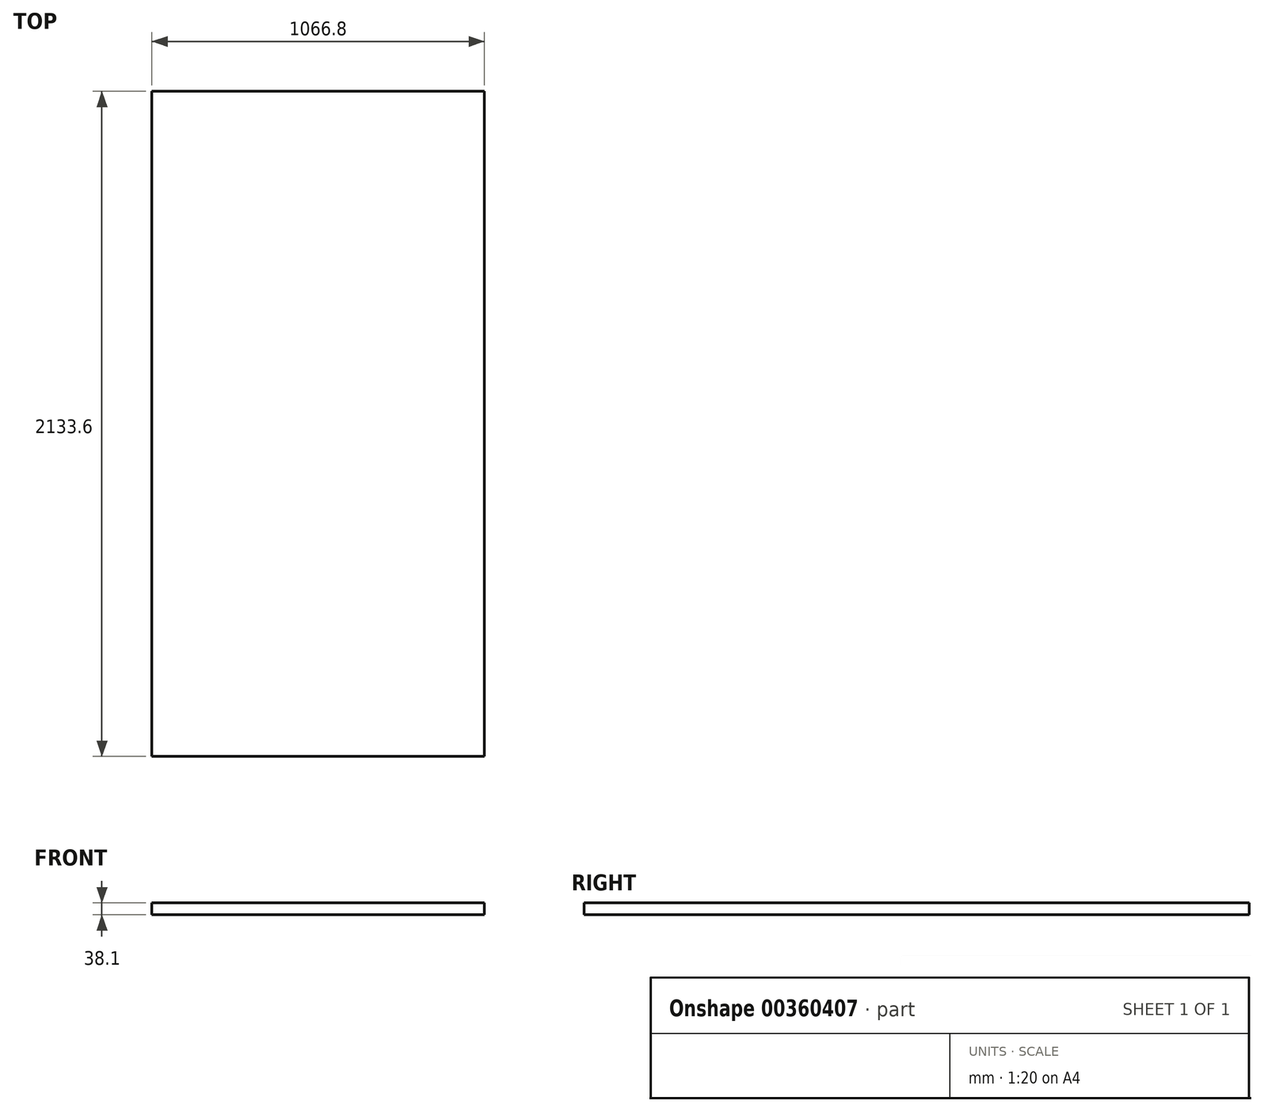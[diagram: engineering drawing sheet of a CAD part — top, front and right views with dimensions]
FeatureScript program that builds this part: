
annotation { "Feature Type Name" : "Feature", "Feature Type Description" : "" }
export const myFeature = defineFeature(function(context is Context, id is Id, definition is map)
    precondition{}
    {
        {
            var Q0;
            Q0=qCreatedBy(makeId("Top.planeOp"),FACE);
            var sketch = newSketch(context, id + "F0", { "sketchPlane" : qUnion([Q0])});
            skLineSegment(sketch, "E0.bottom", {"start": v(533.4, -1066.8) * mm, "end": v(-533.4, -1066.8) * mm});
            skLineSegment(sketch, "E0.top", {"start": v(533.4, 1066.8) * mm, "end": v(-533.4, 1066.8) * mm});
            skLineSegment(sketch, "E0.left", {"start": v(533.4, -1066.8) * mm, "end": v(533.4, 1066.8) * mm});
            skLineSegment(sketch, "E0.right", {"start": v(-533.4, -1066.8) * mm, "end": v(-533.4, 1066.8) * mm});
            skPoint(sketch, "E0.middle", {"position": v(0, 0) * mm});
            skSolve(sketch);
        }
        {
            var Q0;
            Q0=makeQuery(id+"F0.imprint","IMPRINT",FACE,{"disambiguationData":[TD([[makeQuery(id+"F0.imprint","IMPRINT",EDGE,{"derivedFrom":sQuery(id+"F0.wireOp",EDGE,"E0.bottom")}),-1.0]])]});
            var sketch = newSketch(context, id + "F1", { "sketchPlane" : qUnion([Q0])});
            skSolve(sketch);
        }
        {
            var Q0;
            Q0=makeQuery(id+"F1.imprint","IMPRINT",FACE,{"disambiguationData":[TD([[makeQuery(id+"F1.imprint","IMPRINT",EDGE,{"derivedFrom":makeQuery(id+"F0.imprint","IMPRINT",EDGE,{"derivedFrom":sQuery(id+"F0.wireOp",EDGE,"E0.bottom")})}),-1.0]])]});
            var Q1;
            Q1=makeQuery(id+"F0.imprint","IMPRINT",FACE,{"disambiguationData":[TD([[makeQuery(id+"F0.imprint","IMPRINT",EDGE,{"derivedFrom":sQuery(id+"F0.wireOp",EDGE,"E0.bottom")}),-1.0]])]});
            extrude(context, id + "F2", {"entities" : qUnion([Q0, Q1]), "depth" : 38.1 * mm});
        }
        {
            var Q0;
            {var subQ0=sQuery(id+"F0.wireOp",EDGE,"E0.right");var subQ1=sQuery(id+"F0.wireOp",EDGE,"E0.left");var subQ2=sQuery(id+"F0.wireOp",EDGE,"E0.top");var subQ3=sQuery(id+"F0.wireOp",EDGE,"E0.bottom");Q0=makeQuery(id+"F2.opExtrude","SWEPT_BODY",BODY,{"disambiguationData":[OSD([subQ3,subQ2,subQ1,subQ0]),TDD([makeQuery(id+"F1.imprint","IMPRINT",EDGE,{"derivedFrom":makeQuery(id+"F0.imprint","IMPRINT",EDGE,{"derivedFrom":subQ3})}),makeQuery(id+"F1.imprint","IMPRINT",EDGE,{"derivedFrom":makeQuery(id+"F0.imprint","IMPRINT",EDGE,{"derivedFrom":subQ2})}),makeQuery(id+"F1.imprint","IMPRINT",EDGE,{"derivedFrom":makeQuery(id+"F0.imprint","IMPRINT",EDGE,{"derivedFrom":subQ1})}),makeQuery(id+"F1.imprint","IMPRINT",EDGE,{"derivedFrom":makeQuery(id+"F0.imprint","IMPRINT",EDGE,{"derivedFrom":subQ0})})])]});}
            deleteBodies(context, id + "F3", {"entities" : qUnion([Q0])});
        }
    });
